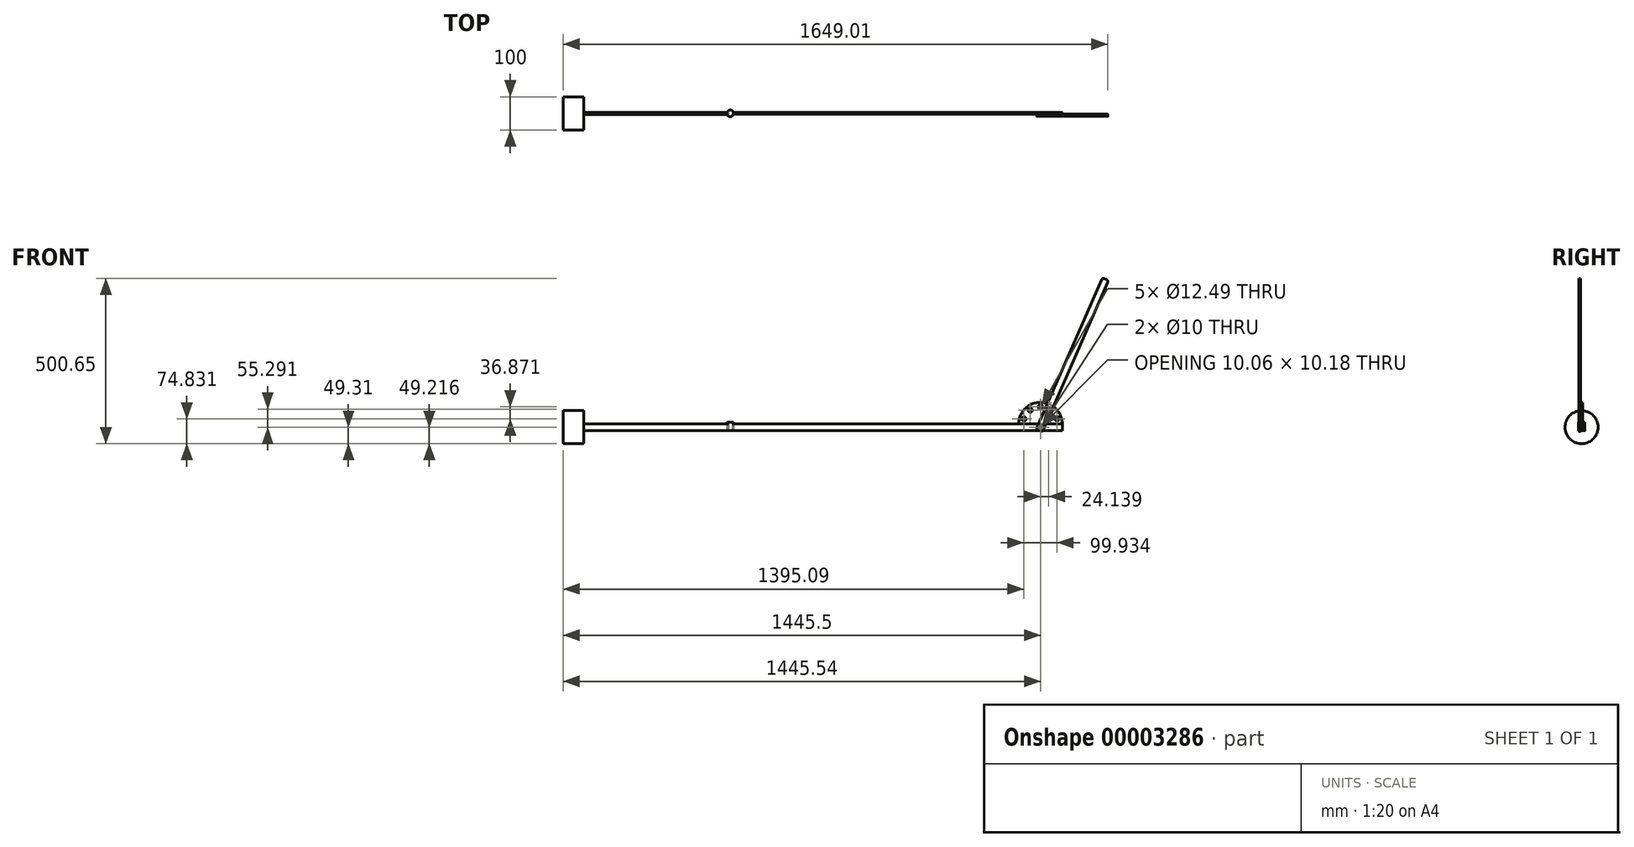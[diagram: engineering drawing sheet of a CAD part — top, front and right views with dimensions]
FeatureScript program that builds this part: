
annotation { "Feature Type Name" : "Feature", "Feature Type Description" : "" }
export const myFeature = defineFeature(function(context is Context, id is Id, definition is map)
    precondition{}
    {
        {
            var Q0;
            Q0=qCreatedBy(makeId("Top.planeOp"),FACE);
            var sketch = newSketch(context, id + "F0", { "sketchPlane" : qUnion([Q0])});
            skLineSegment(sketch, "E0.bottom", {"start": v(5.98, 3.15) * mm, "end": v(1005.98, 3.15) * mm});
            skLineSegment(sketch, "E0.top", {"start": v(5.98, -2.85) * mm, "end": v(1005.98, -2.85) * mm});
            skLineSegment(sketch, "E0.left", {"start": v(5.98, 3.15) * mm, "end": v(5.98, -2.85) * mm});
            skLineSegment(sketch, "E0.right", {"start": v(1005.98, 3.15) * mm, "end": v(1005.98, -2.85) * mm});
            skSolve(sketch);
        }
        {
            var Q0;
            Q0=makeQuery(id+"F0.imprint","IMPRINT",FACE,{"disambiguationData":[TD([[makeQuery(id+"F0.imprint","IMPRINT",EDGE,{"derivedFrom":sQuery(id+"F0.wireOp",EDGE,"E0.bottom")}),-1.0]])]});
            extrude(context, id + "F1", {"entities" : qUnion([Q0]), "depth" : 20 * mm});
        }
        {
            var Q0;
            Q0=qCreatedBy(makeId("Top.planeOp"),FACE);
            var sketch = newSketch(context, id + "F2", { "sketchPlane" : qUnion([Q0])});
            skLineSegment(sketch, "E1.bottom", {"start": v(-5.85, 3.01) * mm, "end": v(-505.85, 3.01) * mm});
            skLineSegment(sketch, "E1.top", {"start": v(-5.85, -2.99) * mm, "end": v(-505.85, -2.99) * mm});
            skLineSegment(sketch, "E1.left", {"start": v(-5.85, 3.01) * mm, "end": v(-5.85, -2.99) * mm});
            skLineSegment(sketch, "E1.right", {"start": v(-505.85, 3.01) * mm, "end": v(-505.85, -2.99) * mm});
            skSolve(sketch);
        }
        {
            var Q0;
            Q0=makeQuery(id+"F2.imprint","IMPRINT",FACE,{"disambiguationData":[TD([[makeQuery(id+"F2.imprint","IMPRINT",EDGE,{"derivedFrom":sQuery(id+"F2.wireOp",EDGE,"E1.bottom")}),1.0]])]});
            extrude(context, id + "F3", {"entities" : qUnion([Q0]), "depth" : 20 * mm});
        }
        {
            var Q0;
            Q0=qCreatedBy(makeId("Top.planeOp"),FACE);
            var sketch = newSketch(context, id + "F4", { "sketchPlane" : qUnion([Q0])});
            skCircle(sketch, "E2", {"center": v(0, 0) * mm, "radius": 10 * mm});
            skSolve(sketch);
        }
        {
            var Q0;
            Q0=makeQuery(id+"F4.imprint","IMPRINT",FACE,{"disambiguationData":[TD([[makeQuery(id+"F4.imprint","IMPRINT",EDGE,{"derivedFrom":sQuery(id+"F4.wireOp",EDGE,"E2")}),1.0]])]});
            extrude(context, id + "F5", {"entities" : qUnion([Q0]), "depth" : 25 * mm});
        }
        {
            var Q0;
            Q0=makeQuery(id+"F1.opExtrude","SWEPT_FACE",FACE,{"disambiguationData":[OSD([sQuery(id+"F0.wireOp",EDGE,"E0.top")])]});
            var sketch = newSketch(context, id + "F6", { "sketchPlane" : qUnion([Q0])});
            skCircle(sketch, "E3", {"center": v(939.69, 10) * mm, "radius": 5 * mm});
            skSolve(sketch);
        }
        {
            var Q0;
            Q0=makeQuery(id+"F6.imprint","IMPRINT",FACE,{"disambiguationData":[TD([[makeQuery(id+"F6.imprint","IMPRINT",EDGE,{"derivedFrom":sQuery(id+"F6.wireOp",EDGE,"E3")}),1.0]])]});
            extrude(context, id + "F7", {"entities" : qUnion([Q0]), "operationType" : NewBodyOperationType.REMOVE, "endBound" : BoundingType.THROUGH_ALL, "oppositeDirection" : true, "depth" : 25 * mm});
        }
        {
            var Q0;
            Q0=makeQuery(id+"F3.opExtrude","SWEPT_FACE",FACE,{"disambiguationData":[OSD([sQuery(id+"F2.wireOp",EDGE,"E1.right")])]});
            var sketch = newSketch(context, id + "F8", { "sketchPlane" : qUnion([Q0])});
            skCircle(sketch, "E4", {"center": v(0, 10.7) * mm, "radius": 50 * mm});
            skSolve(sketch);
        }
        {
            var Q0;
            {var subQ0=sQuery(id+"F2.wireOp",EDGE,"E1.right");var subQ2=makeQuery(id+"F8.imprint","IMPRINT",EDGE,{"derivedFrom":makeQuery(id+"F3.opExtrude","CAP_EDGE",EDGE,{"disambiguationData":[OSD([subQ0])],"isStart":true})});Q0=qUnion([makeQuery(id+"F8.imprint","IMPRINT",FACE,{"disambiguationData":[TD([[makeQuery(id+"F8.imprint","IMPRINT",EDGE,{"derivedFrom":sQuery(id+"F8.wireOp",EDGE,"E4")}),1.0]])]}),makeQuery(id+"F8.imprint","IMPRINT",FACE,{"disambiguationData":[TD([[subQ2,1.0]])]})]);}
            extrude(context, id + "F9", {"entities" : qUnion([Q0]), "operationType" : NewBodyOperationType.ADD, "oppositeDirection" : true, "depth" : 62.33 * mm});
        }
        {
            var Q0;
            Q0=makeQuery(id+"F1.opExtrude","SWEPT_FACE",FACE,{"disambiguationData":[OSD([sQuery(id+"F0.wireOp",EDGE,"E0.top")])]});
            var sketch = newSketch(context, id + "F10", { "sketchPlane" : qUnion([Q0])});
            skArc(sketch, "E5", {"start": v(1005.17, 20) * mm, "mid": v(939.28, 85.89) * mm, "end": v(873.4, 20) * mm});
            skCircle(sketch, "E6", {"center": v(889.24, 35.52) * mm, "radius": 6.25 * mm});
            skSolve(sketch);
        }
        {
            var Q0;
            {var subQ1=sQuery(id+"F10.wireOp",EDGE,"E5");Q0=makeQuery(id+"F10.imprint","IMPRINT",FACE,{"disambiguationData":[TD([[makeQuery(id+"F10.imprint","IMPRINT",EDGE,{"derivedFrom":subQ1}),1.0]])]});}
            extrude(context, id + "F11", {"entities" : qUnion([Q0]), "oppositeDirection" : true, "depth" : 6 * mm});
        }
        {
            var Q0;
            Q0=makeQuery(id+"F11.opExtrude","SWEPT_FACE",FACE,{"disambiguationData":[OSD([sQuery(id+"F10.wireOp",EDGE,"E6")])]});
            var Q1;
            Q1=makeQuery(id+"F11.opExtrude","CAP_EDGE",EDGE,{"disambiguationData":[OSD([sQuery(id+"F10.wireOp",EDGE,"E5")])],"isStart":true});
            circularPattern(context, id + "F12", {"faces" : qUnion([Q0]), "axis" : qUnion([Q1]), "angle" : 145 * degree, "instanceCount" : 5, "oppositeDirection" : true, "equalSpace" : true, "patternType" : PatternType.FACE});
        }
        {
            var Q0;
            Q0=makeQuery(id+"F1.opExtrude","SWEPT_FACE",FACE,{"disambiguationData":[OSD([sQuery(id+"F0.wireOp",EDGE,"E0.top")])]});
            var sketch = newSketch(context, id + "F13", { "sketchPlane" : qUnion([Q0])});
            skLineSegment(sketch, "E7.bottom", {"start": v(944.79, -3.35) * mm, "end": v(926.45, 4.65) * mm});
            skLineSegment(sketch, "E7.top", {"start": v(1144.74, 454.92) * mm, "end": v(1126.41, 462.92) * mm});
            skLineSegment(sketch, "E7.left", {"start": v(944.79, -3.35) * mm, "end": v(1144.74, 454.92) * mm});
            skLineSegment(sketch, "E7.right", {"start": v(926.45, 4.65) * mm, "end": v(1126.41, 462.92) * mm});
            skCircle(sketch, "E8", {"center": v(939.62, 9.81) * mm, "radius": 5 * mm});
            skCircle(sketch, "E9", {"center": v(963.83, 65.3) * mm, "radius": 5 * mm});
            skSolve(sketch);
        }
        {
            var Q0;
            {var subQ5=sQuery(id+"F13.wireOp",EDGE,"E7.top");Q0=makeQuery(id+"F13.imprint","IMPRINT",FACE,{"disambiguationData":[TD([[makeQuery(id+"F13.imprint","IMPRINT",EDGE,{"derivedFrom":subQ5}),1.0]])]});}
            var Q1;
            {var subQ6=sQuery(id+"F13.wireOp",EDGE,"E7.right");var subQ12=sQuery(id+"F13.wireOp",EDGE,"E7.bottom");var subQ14=makeQuery(id+"F13.imprint","INTERSECT",VERTEX,{"derivedFrom":[subQ12,subQ6]});Q1=makeQuery(id+"F13.imprint","IMPRINT",FACE,{"disambiguationData":[TD([[makeQuery(id+"F13.imprint","IMPRINT",EDGE,{"disambiguationData":[TD([[subQ14,1.0]])],"derivedFrom":subQ12}),-1.0]])]});}
            var Q2;
            {var subQ1=sQuery(id+"F13.wireOp",EDGE,"E7.left");var subQ3=sQuery(id+"F13.wireOp",EDGE,"E7.bottom");var subQ5=makeQuery(id+"F13.imprint","INTERSECT",VERTEX,{"derivedFrom":[subQ3,subQ1]});Q2=makeQuery(id+"F13.imprint","IMPRINT",FACE,{"disambiguationData":[TD([[makeQuery(id+"F13.imprint","IMPRINT",EDGE,{"disambiguationData":[TD([[subQ5,-1.0]])],"derivedFrom":subQ3}),-1.0]])]});}
            extrude(context, id + "F14", {"entities" : qUnion([Q0, Q1, Q2]), "depth" : 6 * mm});
        }
        {
            var Q0;
            Q0=makeQuery(id+"F14.opExtrude","SWEPT_EDGE",EDGE,{"disambiguationData":[OSD([sQuery(id+"F13.wireOp",EDGE,"E7.bottom"),sQuery(id+"F13.wireOp",EDGE,"E7.right")])]});
            var Q1;
            Q1=makeQuery(id+"F14.opExtrude","SWEPT_EDGE",EDGE,{"disambiguationData":[OSD([sQuery(id+"F13.wireOp",EDGE,"E7.bottom"),sQuery(id+"F13.wireOp",EDGE,"E7.left")])]});
            var Q2;
            Q2=makeQuery(id+"F14.opExtrude","SWEPT_EDGE",EDGE,{"disambiguationData":[OSD([sQuery(id+"F13.wireOp",EDGE,"E7.top"),sQuery(id+"F13.wireOp",EDGE,"E7.left")])]});
            var Q3;
            Q3=makeQuery(id+"F14.opExtrude","SWEPT_EDGE",EDGE,{"disambiguationData":[OSD([sQuery(id+"F13.wireOp",EDGE,"E7.top"),sQuery(id+"F13.wireOp",EDGE,"E7.right")])]});
            fillet(context, id + "F15", {"entities" : qUnion([Q0, Q1, Q2, Q3]), "radius" : 5 * mm, "tangentPropagation" : true, "allowEdgeOverflow" : false});
        }
    });
